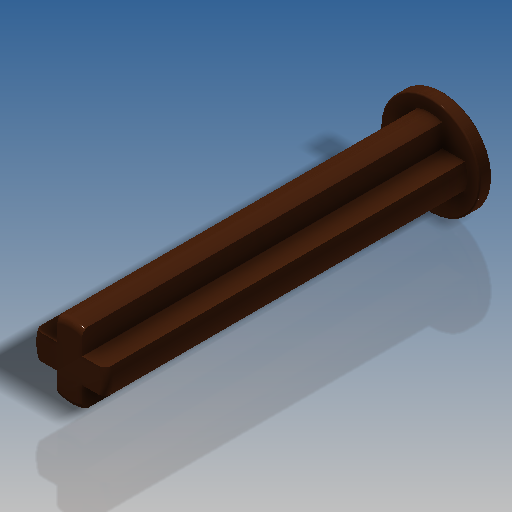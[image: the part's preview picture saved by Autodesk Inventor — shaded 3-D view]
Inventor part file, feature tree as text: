
AUTODESK INVENTOR PART (.ipt)
format: ipt  version: 2019.4 (Build 234330000, 330)  size: 219,136 bytes
history: native  units: in
note: dims shown in document units (in); Inventor stores cm internally (conversion verified against a paired STEP export)
features: extrude x2, sketch x2, fillet x1
ambient origin geometry x8: Origin, YZ Plane, XZ Plane, XY Plane, X Axis, Y Axis, Z Axis, Center Point
bodies: Solid1 (feature_tree)
feature tree (5):
  extrude  "Extrusion1"  Depth=0.063in
  extrude  "Extrusion2"  TaperAngle=0.0deg  [1 undecoded]
  fillet  "Fillet1"  Radius=0.0157in
  sketch  "Sketch1"  dims[d0=0.189in d1=0.063in]
  sketch  "Sketch2"  dims[d2=0.9449in d3=0.0in d4=0.0157in d7=0.252in d8=0.0315in d9=0.0in d10=0.0039in d11=0.0in d12=0.0in]
note: 1 required parameter value undecoded (feature->parameter linkage not recoverable at this tier; creation-order binding heuristic only, values carry confidence <= 0.55)
